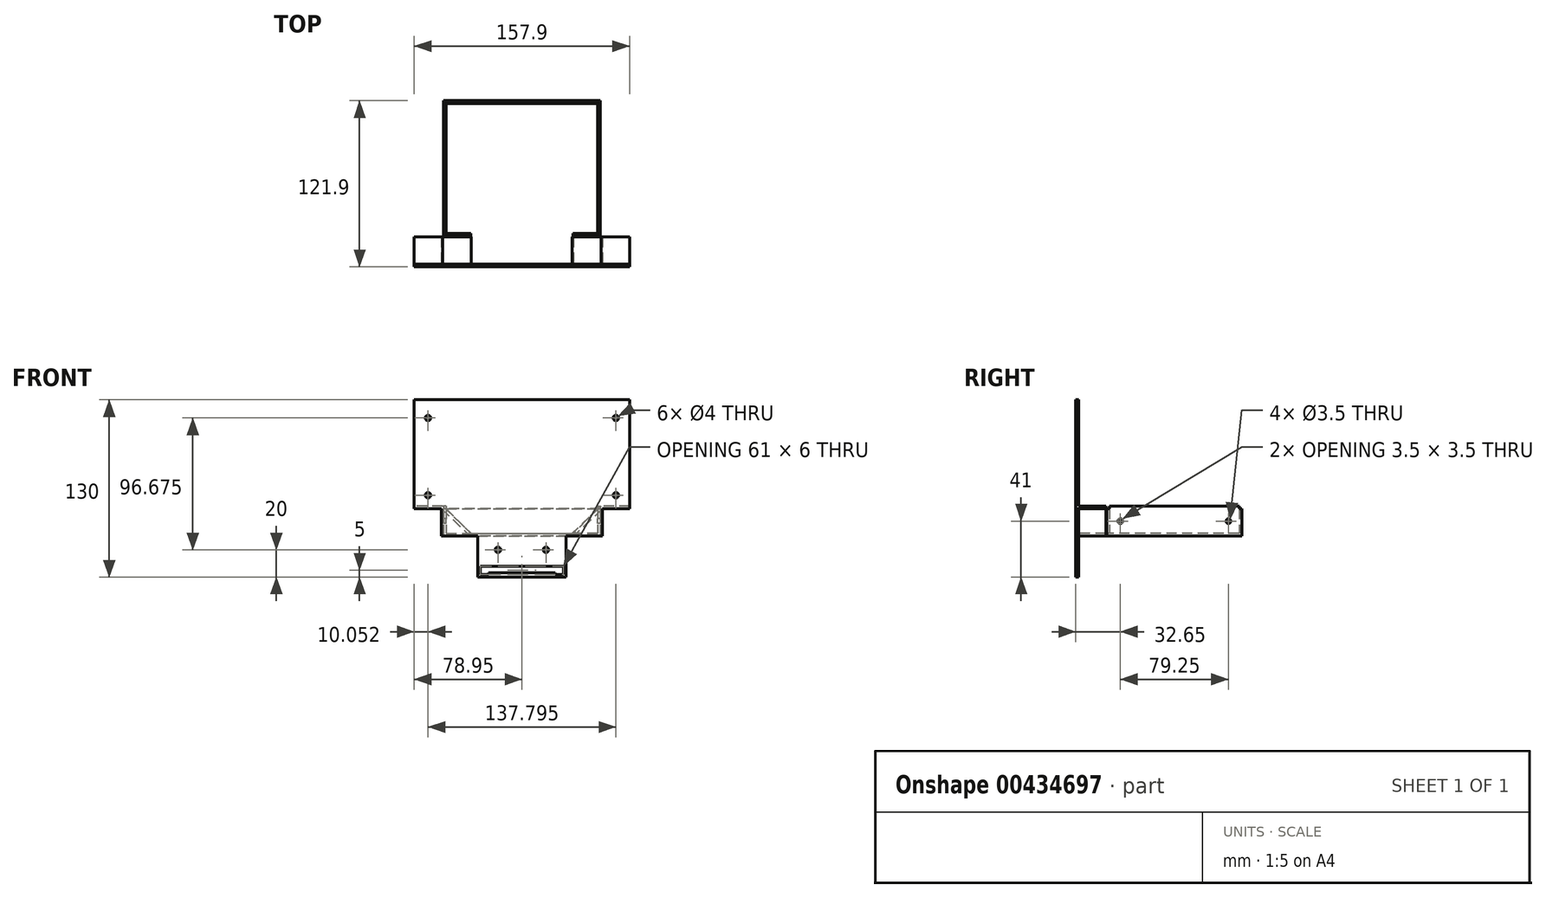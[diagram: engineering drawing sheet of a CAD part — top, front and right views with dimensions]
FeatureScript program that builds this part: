
annotation { "Feature Type Name" : "Feature", "Feature Type Description" : "" }
export const myFeature = defineFeature(function(context is Context, id is Id, definition is map)
    precondition{}
    {
        {
            assignVariable(context, id + "F0", {"name" : "Thickness", "anyValue" : 2});
        }
        {
            var Q0;
            Q0=qCreatedBy(makeId("Top.planeOp"),FACE);
            var sketch = newSketch(context, id + "F1", { "sketchPlane" : qUnion([Q0])});
            skLineSegment(sketch, "E0", {"start": v(-80.9, 0) * mm, "end": v(80.9, 0) * mm, "construction": true});
            skLineSegment(sketch, "E1", {"start": v(0, 80.9) * mm, "end": v(0, -80.9) * mm, "construction": true});
            skLineSegment(sketch, "E2", {"start": v(-37.5, -73.73) * mm, "end": v(37.5, -73.73) * mm, "construction": true});
            skLineSegment(sketch, "E3", {"start": v(95.64, -60) * mm, "end": v(95.64, 60) * mm, "construction": true});
            skLineSegment(sketch, "E4", {"start": v(37.5, -60) * mm, "end": v(-37.5, -60) * mm});
            skLineSegment(sketch, "E5", {"start": v(-37.5, -60) * mm, "end": v(-37.5, -39.25) * mm});
            skLineSegment(sketch, "E6", {"start": v(-37.5, -39.25) * mm, "end": v(-57.5, -39.25) * mm});
            skLineSegment(sketch, "E7", {"start": v(-57.5, -39.25) * mm, "end": v(-57.5, 60) * mm});
            skLineSegment(sketch, "E8", {"start": v(-57.5, 60) * mm, "end": v(0, 60) * mm});
            skLineSegment(sketch, "E9.MirrorCS", {"start": v(57.5, 60) * mm, "end": v(0, 60) * mm});
            skLineSegment(sketch, "E10.MirrorCS", {"start": v(57.5, -39.25) * mm, "end": v(57.5, 60) * mm});
            skLineSegment(sketch, "E11.MirrorCS", {"start": v(37.5, -39.25) * mm, "end": v(57.5, -39.25) * mm});
            skLineSegment(sketch, "E12.MirrorCS", {"start": v(37.5, -60) * mm, "end": v(37.5, -39.25) * mm});
            skSolve(sketch);
        }
        {
            var Q0;
            Q0=qSketchRegion(id+"F1",true);
            var Q1;
            Q1=qConstructionFilter(qBodyType(qCreatedBy(id+"F1",EDGE),BodyType.WIRE),ConstructionObject.NO);
            extrude(context, id + "F2", {"entities" : qUnion([Q0]), "surfaceEntities" : qUnion([Q1]), "depth" : (getVariable(context, 'Thickness')) * mm});
        }
        {
            var Q0;
            Q0=makeQuery(id+"F2.opExtrude","CAP_FACE",FACE,{"disambiguationData":[OSD([sQuery(id+"F1.wireOp",EDGE,"E4"),sQuery(id+"F1.wireOp",EDGE,"E5"),sQuery(id+"F1.wireOp",EDGE,"E6"),sQuery(id+"F1.wireOp",EDGE,"E7"),sQuery(id+"F1.wireOp",EDGE,"E8"),sQuery(id+"F1.wireOp",EDGE,"E9.MirrorCS"),sQuery(id+"F1.wireOp",EDGE,"E10.MirrorCS"),sQuery(id+"F1.wireOp",EDGE,"E11.MirrorCS"),sQuery(id+"F1.wireOp",EDGE,"E12.MirrorCS")])],"isStart":false});
            var sketch = newSketch(context, id + "F3", { "sketchPlane" : qUnion([Q0])});
            skLineSegment(sketch, "E13", {"start": v(-55.5, 58) * mm, "end": v(-55.5, -37.25) * mm});
            skLineSegment(sketch, "E14", {"start": v(-55.5, 58) * mm, "end": v(55.5, 58) * mm});
            skLineSegment(sketch, "E15", {"start": v(55.5, 58) * mm, "end": v(55.5, -37.25) * mm});
            skLineSegment(sketch, "E16", {"start": v(-55.5, -37.25) * mm, "end": v(-57.5, -37.25) * mm, "construction": true});
            skLineSegment(sketch, "E17", {"start": v(55.5, -37.25) * mm, "end": v(57.5, -37.25) * mm, "construction": true});
            skLineSegment(sketch, "E18.0", {"start": v(-57.5, -39.25) * mm, "end": v(-57.5, 60) * mm});
            skLineSegment(sketch, "E18.1", {"start": v(-57.5, 60) * mm, "end": v(0, 60) * mm});
            skLineSegment(sketch, "E18.2", {"start": v(57.5, 60) * mm, "end": v(0, 60) * mm});
            skLineSegment(sketch, "E18.3", {"start": v(57.5, -39.25) * mm, "end": v(57.5, 60) * mm});
            skLineSegment(sketch, "E19.0", {"start": v(-37.5, -39.25) * mm, "end": v(-57.5, -39.25) * mm});
            skLineSegment(sketch, "E19.1", {"start": v(37.5, -39.25) * mm, "end": v(57.5, -39.25) * mm});
            skLineSegment(sketch, "E20", {"start": v(-55.5, -37.25) * mm, "end": v(-37.5, -37.25) * mm});
            skLineSegment(sketch, "E21", {"start": v(-37.5, -37.25) * mm, "end": v(-37.5, -39.25) * mm});
            skLineSegment(sketch, "E22", {"start": v(55.5, -37.25) * mm, "end": v(37.5, -37.25) * mm});
            skLineSegment(sketch, "E23", {"start": v(37.5, -37.25) * mm, "end": v(37.5, -39.25) * mm});
            skSolve(sketch);
        }
        {
            var Q0;
            Q0=makeQuery(id+"F3.imprint","IMPRINT",FACE,{"disambiguationData":[TD([[makeQuery(id+"F3.imprint","IMPRINT",EDGE,{"derivedFrom":sQuery(id+"F3.wireOp",EDGE,"E13")}),-1.0]])]});
            extrude(context, id + "F4", {"entities" : qUnion([Q0]), "operationType" : NewBodyOperationType.ADD, "depth" : (20 - getVariable(context, 'Thickness')) * mm});
        }
        {
            var Q0;
            Q0=makeQuery(id+"F4.boolean.opBoolean","MERGE",FACE,{"derivedFrom":[makeQuery(id+"F2.opExtrude","SWEPT_FACE",FACE,{"disambiguationData":[OSD([sQuery(id+"F1.wireOp",EDGE,"E6")])]}),makeQuery(id+"F4.opExtrude","SWEPT_FACE",FACE,{"disambiguationData":[OSD([sQuery(id+"F3.wireOp",EDGE,"E19.0")])]})]});
            var sketch = newSketch(context, id + "F5", { "sketchPlane" : qUnion([Q0])});
            skLineSegment(sketch, "E24.0", {"start": v(-37.5, 20) * mm, "end": v(-57.5, 20) * mm});
            skLineSegment(sketch, "E24.1", {"start": v(37.5, 20) * mm, "end": v(57.5, 20) * mm});
            skLineSegment(sketch, "E24.2", {"start": v(-37.5, 20) * mm, "end": v(-37.5, 2) * mm});
            skLineSegment(sketch, "E24.3", {"start": v(37.5, 20) * mm, "end": v(37.5, 2) * mm});
            skLineSegment(sketch, "E25", {"start": v(-55.5, 20) * mm, "end": v(-37.5, 2) * mm});
            skLineSegment(sketch, "E26", {"start": v(0, 0) * mm, "end": v(0, 28.5) * mm, "construction": true});
            skLineSegment(sketch, "E27.MirrorCS", {"start": v(55.5, 20) * mm, "end": v(37.5, 2) * mm});
            skSolve(sketch);
        }
        {
            var Q0;
            {var subQ0=sQuery(id+"F5.wireOp",EDGE,"E24.2");Q0=makeQuery(id+"F5.imprint","IMPRINT",FACE,{"disambiguationData":[TD([[makeQuery(id+"F5.imprint","IMPRINT",EDGE,{"derivedFrom":subQ0}),-1.0]])]});}
            var Q1;
            {var subQ0=sQuery(id+"F5.wireOp",EDGE,"E24.3");Q1=makeQuery(id+"F5.imprint","IMPRINT",FACE,{"disambiguationData":[TD([[makeQuery(id+"F5.imprint","IMPRINT",EDGE,{"derivedFrom":subQ0}),1.0]])]});}
            var Q2;
            Q2=makeQuery(id+"F4.opExtrude","SWEPT_FACE",FACE,{"disambiguationData":[OSD([sQuery(id+"F3.wireOp",EDGE,"E20")])]});
            extrude(context, id + "F6", {"entities" : qUnion([Q0, Q1]), "operationType" : NewBodyOperationType.REMOVE, "endBound" : BoundingType.UP_TO_SURFACE, "oppositeDirection" : true, "endBoundEntityFace" : qUnion([Q2]), "depth" : 25 * mm});
        }
        {
            var Q0;
            Q0=makeQuery(id+"F4.boolean.opBoolean","MERGE",FACE,{"derivedFrom":[makeQuery(id+"F2.opExtrude","SWEPT_FACE",FACE,{"disambiguationData":[OSD([sQuery(id+"F1.wireOp",EDGE,"E7")])]}),makeQuery(id+"F4.opExtrude","SWEPT_FACE",FACE,{"disambiguationData":[OSD([sQuery(id+"F3.wireOp",EDGE,"E18.0")])]})]});
            var sketch = newSketch(context, id + "F7", { "sketchPlane" : qUnion([Q0])});
            skCircle(sketch, "E28", {"center": v(-50, 11) * mm, "radius": 1.75 * mm});
            skCircle(sketch, "E29", {"center": v(29.25, 11) * mm, "radius": 1.75 * mm});
            skSolve(sketch);
        }
        {
            var Q0;
            Q0=qSketchRegion(id+"F7",true);
            extrude(context, id + "F8", {"entities" : qUnion([Q0]), "operationType" : NewBodyOperationType.REMOVE, "endBound" : BoundingType.THROUGH_ALL, "oppositeDirection" : true, "depth" : 25 * mm});
        }
        {
            var Q0;
            Q0=makeQuery(id+"F4.opExtrude","CAP_FACE",FACE,{"disambiguationData":[OSD([sQuery(id+"F3.wireOp",EDGE,"E13"),sQuery(id+"F3.wireOp",EDGE,"E14"),sQuery(id+"F3.wireOp",EDGE,"E15"),sQuery(id+"F3.wireOp",EDGE,"E18.0"),sQuery(id+"F3.wireOp",EDGE,"E18.1"),sQuery(id+"F3.wireOp",EDGE,"E18.2"),sQuery(id+"F3.wireOp",EDGE,"E18.3"),sQuery(id+"F3.wireOp",EDGE,"E19.0"),sQuery(id+"F3.wireOp",EDGE,"E19.1"),sQuery(id+"F3.wireOp",EDGE,"E20"),sQuery(id+"F3.wireOp",EDGE,"E21"),sQuery(id+"F3.wireOp",EDGE,"E22"),sQuery(id+"F3.wireOp",EDGE,"E23")])],"isStart":false});
            var sketch = newSketch(context, id + "F9", { "sketchPlane" : qUnion([Q0])});
            skLineSegment(sketch, "E30.0", {"start": v(57.5, -39.25) * mm, "end": v(57.5, 60) * mm});
            skLineSegment(sketch, "E30.1", {"start": v(55.5, 58) * mm, "end": v(55.5, -37.25) * mm});
            skLineSegment(sketch, "E30.2", {"start": v(-55.5, 58) * mm, "end": v(-55.5, -37.25) * mm});
            skLineSegment(sketch, "E30.3", {"start": v(-57.5, -39.25) * mm, "end": v(-57.5, 60) * mm});
            skLineSegment(sketch, "E31", {"start": v(55.5, 58) * mm, "end": v(57.5, 58) * mm});
            skLineSegment(sketch, "E32", {"start": v(55.5, -37.25) * mm, "end": v(57.5, -37.25) * mm});
            skLineSegment(sketch, "E33", {"start": v(-55.5, -37.25) * mm, "end": v(-57.5, -37.25) * mm});
            skLineSegment(sketch, "E34", {"start": v(-55.5, 58) * mm, "end": v(-57.5, 58) * mm});
            skSolve(sketch);
        }
        {
            var Q0;
            Q0=qSketchRegion(id+"F9",true);
            extrude(context, id + "F10", {"entities" : qUnion([Q0]), "operationType" : NewBodyOperationType.ADD, "depth" : (getVariable(context, 'Thickness')) * mm});
        }
        {
            var Q0;
            Q0=qCreatedBy(makeId("Front.planeOp"),FACE);
            cPlane(context, id + "F11", {"entities" : qUnion([Q0]), "cplaneType" : CPlaneType.OFFSET, "offset" : 59.9 * mm, "width" : 150 * mm, "height" : 150 * mm});
        }
        {
            var Q0;
            Q0=qCreatedBy(id+"F11.planeOp",FACE);
            var sketch = newSketch(context, id + "F12", { "sketchPlane" : qUnion([Q0])});
            skLineSegment(sketch, "E35", {"start": v(0, 49.3) * mm, "end": v(0, -45.27) * mm, "construction": true});
            skLineSegment(sketch, "E36", {"start": v(-32.5, -30) * mm, "end": v(32.5, -30) * mm});
            skLineSegment(sketch, "E37", {"start": v(-32.5, -30) * mm, "end": v(-32.5, 0) * mm});
            skLineSegment(sketch, "E38", {"start": v(32.5, -30) * mm, "end": v(32.5, 0) * mm});
            skLineSegment(sketch, "E39", {"start": v(-58.95, 0) * mm, "end": v(-58.95, 20) * mm});
            skLineSegment(sketch, "E40", {"start": v(58.95, 20) * mm, "end": v(58.95, 0) * mm});
            skLineSegment(sketch, "E41", {"start": v(-58.95, 20) * mm, "end": v(-78.95, 20) * mm});
            skLineSegment(sketch, "E42", {"start": v(-78.95, 20) * mm, "end": v(-78.95, 100) * mm});
            skLineSegment(sketch, "E43", {"start": v(-78.95, 100) * mm, "end": v(0, 100) * mm});
            skLineSegment(sketch, "E44.MirrorCS", {"start": v(58.95, 20) * mm, "end": v(78.95, 20) * mm});
            skLineSegment(sketch, "E45.MirrorCS", {"start": v(78.95, 20) * mm, "end": v(78.95, 100) * mm});
            skLineSegment(sketch, "E46.MirrorCS", {"start": v(78.95, 100) * mm, "end": v(0, 100) * mm});
            skCircle(sketch, "E47", {"center": v(-68.9, 86.67) * mm, "radius": 2 * mm});
            skCircle(sketch, "E48", {"center": v(-68.9, 30) * mm, "radius": 2 * mm});
            skCircle(sketch, "E49", {"center": v(-17.6, -10) * mm, "radius": 2 * mm});
            skLineSegment(sketch, "E50.bottom", {"start": v(-30.5, -27) * mm, "end": v(-24.5, -27) * mm});
            skLineSegment(sketch, "E50.top", {"start": v(-30.5, -22) * mm, "end": v(30.5, -22) * mm});
            skLineSegment(sketch, "E50.left", {"start": v(-30.5, -27) * mm, "end": v(-30.5, -22) * mm});
            skLineSegment(sketch, "E50.right", {"start": v(30.5, -27) * mm, "end": v(30.5, -22) * mm});
            skCircle(sketch, "E51.MirrorC", {"center": v(68.9, 86.67) * mm, "radius": 2 * mm});
            skCircle(sketch, "E52.MirrorC", {"center": v(68.9, 30) * mm, "radius": 2 * mm});
            skCircle(sketch, "E53.MirrorC", {"center": v(17.6, -10) * mm, "radius": 2 * mm});
            skLineSegment(sketch, "E54.bottom", {"start": v(-30.5, -27) * mm, "end": v(-24.5, -27) * mm, "construction": true});
            skLineSegment(sketch, "E54.top", {"start": v(-30.5, -28) * mm, "end": v(-24.5, -28) * mm});
            skLineSegment(sketch, "E54.left", {"start": v(-30.5, -27) * mm, "end": v(-30.5, -28) * mm});
            skLineSegment(sketch, "E54.right", {"start": v(-24.5, -27) * mm, "end": v(-24.5, -28) * mm});
            skLineSegment(sketch, "E55.MirrorCS", {"start": v(24.5, -27) * mm, "end": v(24.5, -28) * mm});
            skLineSegment(sketch, "E56.MirrorCS", {"start": v(30.5, -28) * mm, "end": v(24.5, -28) * mm});
            skLineSegment(sketch, "E57.MirrorCS", {"start": v(30.5, -27) * mm, "end": v(30.5, -28) * mm});
            skLineSegment(sketch, "E58", {"start": v(-24.5, -27) * mm, "end": v(24.5, -27) * mm});
            skLineSegment(sketch, "E59", {"start": v(24.5, -27) * mm, "end": v(30.5, -27) * mm, "construction": true});
            skLineSegment(sketch, "E60.1", {"start": v(-37.5, 20) * mm, "end": v(-57.5, 20) * mm, "construction": true});
            skLineSegment(sketch, "E61", {"start": v(-55.5, 20) * mm, "end": v(-55.5, 22) * mm, "construction": true});
            skLineSegment(sketch, "E62", {"start": v(-55.5, 22) * mm, "end": v(-58.15, 22) * mm, "construction": true});
            skLineSegment(sketch, "E63", {"start": v(-40.46, 22) * mm, "end": v(-55.5, 22) * mm, "construction": true});
            skLineSegment(sketch, "E64", {"start": v(-32.5, -0.14) * mm, "end": v(-29.72, -0.14) * mm});
            skLineSegment(sketch, "E65", {"start": v(-58.15, 22) * mm, "end": v(-78.95, 22) * mm});
            skLineSegment(sketch, "E66.MirrorCS", {"start": v(58.12, 22.16) * mm, "end": v(34.82, 0) * mm});
            skLineSegment(sketch, "E67.MirrorCS", {"start": v(58.15, 22) * mm, "end": v(78.95, 22) * mm});
            skLineSegment(sketch, "E68", {"start": v(58.95, 0) * mm, "end": v(32.5, 0) * mm});
            skLineSegment(sketch, "E69", {"start": v(-58.95, 0) * mm, "end": v(-32.5, 0) * mm});
            skLineSegment(sketch, "E70", {"start": v(58.95, 20) * mm, "end": v(37.91, 0) * mm});
            skLineSegment(sketch, "E71.MirrorCS", {"start": v(-58.95, 20) * mm, "end": v(-37.91, 0) * mm});
            skLineSegment(sketch, "E72.MirrorCS", {"start": v(55.5, 22) * mm, "end": v(58.15, 22) * mm, "construction": true});
            skLineSegment(sketch, "E73", {"start": v(-58.15, 22) * mm, "end": v(-35, 0) * mm});
            skLineSegment(sketch, "E74", {"start": v(37.91, 0) * mm, "end": v(34.82, 0) * mm});
            skLineSegment(sketch, "E75", {"start": v(78.95, 20) * mm, "end": v(78.95, 22) * mm});
            skLineSegment(sketch, "E76", {"start": v(-78.95, 20) * mm, "end": v(-78.95, 22) * mm});
            skLineSegment(sketch, "E77", {"start": v(-78.95, 22) * mm, "end": v(-58.15, 22) * mm});
            skLineSegment(sketch, "E78", {"start": v(-35, 0) * mm, "end": v(-37.91, 0) * mm});
            skLineSegment(sketch, "E79", {"start": v(-37.91, 0) * mm, "end": v(-58.95, 20) * mm});
            skLineSegment(sketch, "E80", {"start": v(58.15, 22) * mm, "end": v(57.96, 22) * mm});
            skSolve(sketch);
        }
        {
            var Q0;
            Q0=qSketchRegion(id+"F12",true);
            extrude(context, id + "F13", {"entities" : qUnion([Q0]), "depth" : (getVariable(context, 'Thickness')) * mm});
        }
        {
            var Q0;
            Q0=makeQuery(id+"F12.imprint","IMPRINT",FACE,{"disambiguationData":[TD([[makeQuery(id+"F12.imprint","IMPRINT",EDGE,{"derivedFrom":sQuery(id+"F12.wireOp",EDGE,"E70")}),-1.0]])]});
            var Q1;
            Q1=makeQuery(id+"F12.imprint","IMPRINT",FACE,{"disambiguationData":[TD([[makeQuery(id+"F12.imprint","IMPRINT",EDGE,{"derivedFrom":sQuery(id+"F12.wireOp",EDGE,"E41")}),-1.0]])]});
            extrude(context, id + "F14", {"entities" : qUnion([Q0, Q1]), "operationType" : NewBodyOperationType.ADD, "oppositeDirection" : true, "depth" : 20 * mm});
        }
    });
